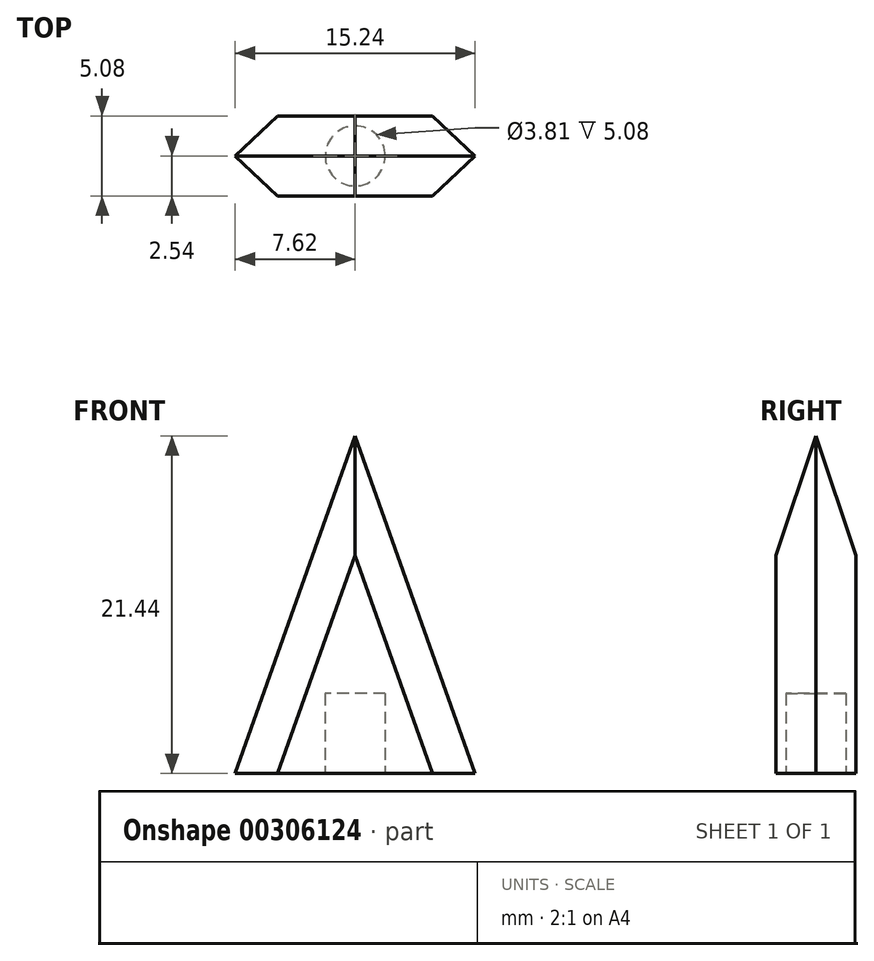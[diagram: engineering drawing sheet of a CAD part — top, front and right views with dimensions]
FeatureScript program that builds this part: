
annotation { "Feature Type Name" : "Feature", "Feature Type Description" : "" }
export const myFeature = defineFeature(function(context is Context, id is Id, definition is map)
    precondition{}
    {
        {
            var Q0;
            Q0=qCreatedBy(makeId("Front.planeOp"),FACE);
            var sketch = newSketch(context, id + "F0", { "sketchPlane" : qUnion([Q0])});
            skLineSegment(sketch, "E0", {"start": v(-7.62, 0) * mm, "end": v(0, 21.44) * mm});
            skLineSegment(sketch, "E1", {"start": v(0, 21.44) * mm, "end": v(7.62, 0) * mm});
            skLineSegment(sketch, "E2", {"start": v(-7.62, 0) * mm, "end": v(7.62, 0) * mm});
            skSolve(sketch);
        }
        {
            var Q0;
            Q0=makeQuery(id+"F0.imprint","IMPRINT",FACE,{"disambiguationData":[TD([[makeQuery(id+"F0.imprint","IMPRINT",EDGE,{"derivedFrom":sQuery(id+"F0.wireOp",EDGE,"E0")}),-1.0]])]});
            extrude(context, id + "F1", {"entities" : qUnion([Q0]), "depth" : 2.54 * mm, "hasSecondDirection" : true, "secondDirectionOppositeDirection" : true, "secondDirectionDepth" : 2.54 * mm});
        }
        {
            var Q0;
            Q0=qCreatedBy(makeId("Top.planeOp"),FACE);
            var sketch = newSketch(context, id + "F2", { "sketchPlane" : qUnion([Q0])});
            skCircle(sketch, "E3", {"center": v(0, 0) * mm, "radius": 1.9 * mm});
            skSolve(sketch);
        }
        {
            var Q0;
            Q0 = qSketchRegion(id + "F2", true);
            extrude(context, id + "F3", {"entities" : qUnion([Q0]), "operationType" : NewBodyOperationType.REMOVE, "depth" : 5.08 * mm});
        }
        {
            var Q0;
            Q0=makeQuery(id+"F1.opExtrude","CAP_EDGE",EDGE,{"disambiguationData":[OSD([sQuery(id+"F0.wireOp",EDGE,"E1")])],"isStart":false});
            var Q1;
            Q1=makeQuery(id+"F1.opExtrude","CAP_EDGE",EDGE,{"disambiguationData":[OSD([sQuery(id+"F0.wireOp",EDGE,"E0")])],"isStart":false});
            var Q2;
            Q2=makeQuery(id+"F1.opExtrude","CAP_EDGE",EDGE,{"disambiguationData":[OSD([sQuery(id+"F0.wireOp",EDGE,"E0")])],"isStart":true});
            var Q3;
            Q3=makeQuery(id+"F1.opExtrude","CAP_EDGE",EDGE,{"disambiguationData":[OSD([sQuery(id+"F0.wireOp",EDGE,"E1")])],"isStart":true});
            chamfer(context, id + "F4", {"entities" : qUnion([Q0, Q1, Q2, Q3]), "width" : 2.54 * mm, "tangentPropagation" : true});
        }
    });
